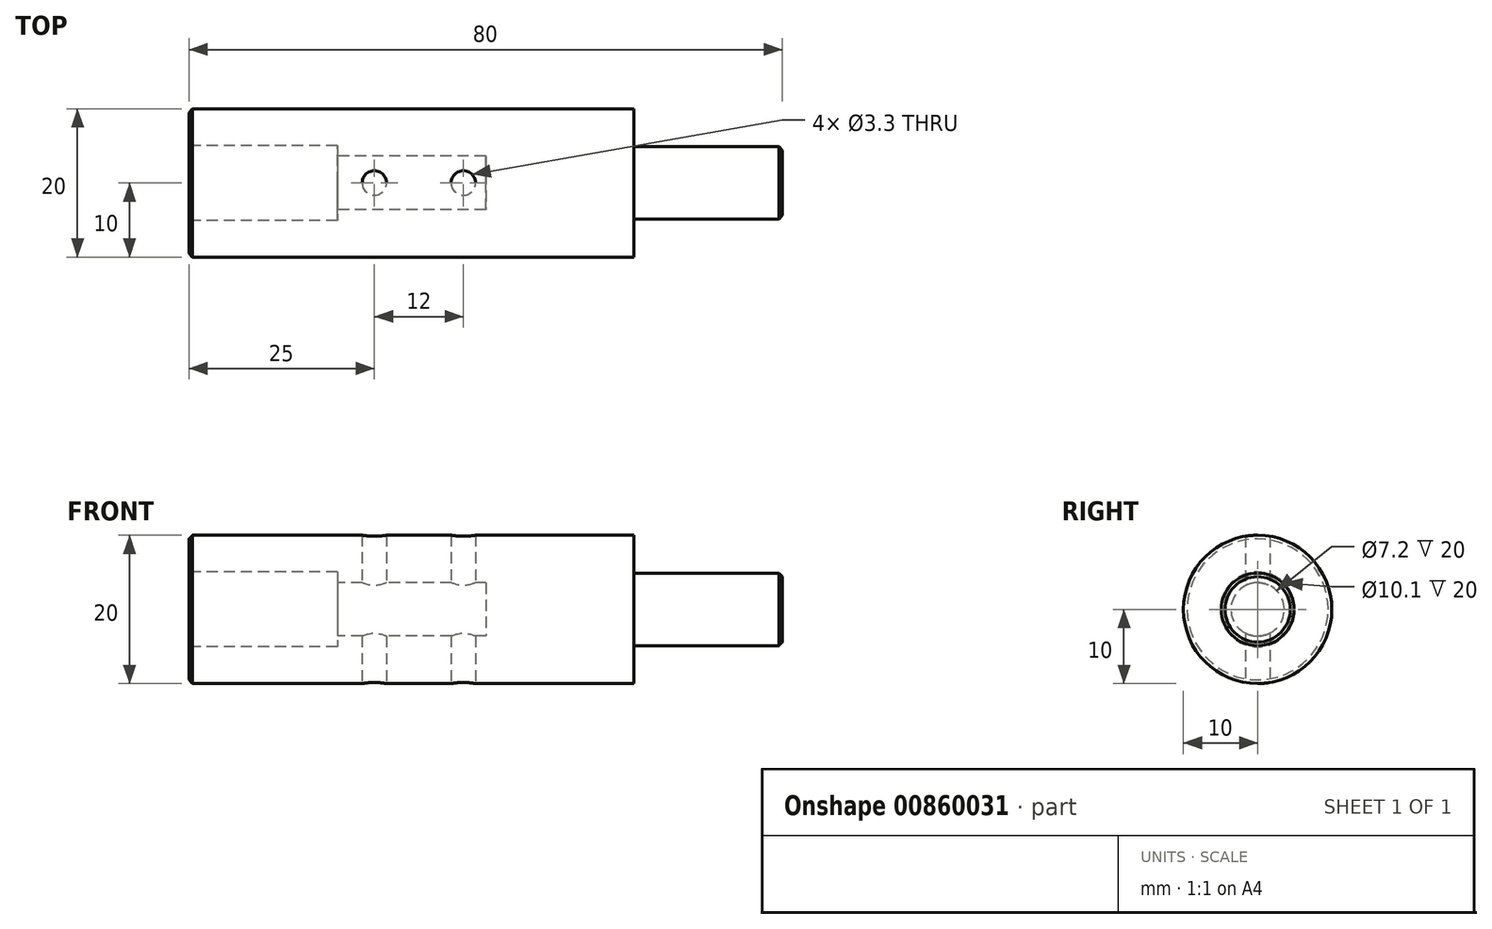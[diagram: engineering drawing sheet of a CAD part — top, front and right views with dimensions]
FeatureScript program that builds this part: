
annotation { "Feature Type Name" : "Feature", "Feature Type Description" : "" }
export const myFeature = defineFeature(function(context is Context, id is Id, definition is map)
    precondition{}
    {
        {
            var Q0;
            Q0=qCreatedBy(makeId("Front.planeOp"),FACE);
            var sketch = newSketch(context, id + "F0", { "sketchPlane" : qUnion([Q0])});
            skLineSegment(sketch, "E0", {"start": v(0, 0) * mm, "end": v(0, 3.6) * mm});
            skLineSegment(sketch, "E1", {"start": v(0, 3.6) * mm, "end": v(-20, 3.6) * mm});
            skLineSegment(sketch, "E2", {"start": v(-20, 3.6) * mm, "end": v(-20, 5.05) * mm});
            skLineSegment(sketch, "E3", {"start": v(-20, 5.05) * mm, "end": v(-40, 5.05) * mm});
            skLineSegment(sketch, "E4", {"start": v(-40, 5.05) * mm, "end": v(-40, 10) * mm});
            skLineSegment(sketch, "E5", {"start": v(-40, 10) * mm, "end": v(20, 10) * mm});
            skLineSegment(sketch, "E6", {"start": v(20, 10) * mm, "end": v(20, 4.9) * mm});
            skLineSegment(sketch, "E7", {"start": v(20, 4.9) * mm, "end": v(40, 4.9) * mm});
            skLineSegment(sketch, "E8", {"start": v(40, 4.9) * mm, "end": v(40, 0) * mm});
            skLineSegment(sketch, "E9", {"start": v(40, 0) * mm, "end": v(0, 0) * mm});
            skLineSegment(sketch, "E10", {"start": v(-51.87, 0) * mm, "end": v(49.04, 0) * mm, "construction": true});
            skSolve(sketch);
        }
        {
            var Q0;
            Q0=makeQuery(id+"F0.imprint","IMPRINT",FACE,{"disambiguationData":[TD([[makeQuery(id+"F0.imprint","IMPRINT",EDGE,{"derivedFrom":sQuery(id+"F0.wireOp",EDGE,"E0")}),-1.0]])]});
            var Q1;
            Q1=sQuery(id+"F0.wireOp",EDGE,"E10");
            revolve(context, id + "F1", {"surfaceOperationType" : NewSurfaceOperationType.NEW, "entities" : qUnion([Q0]), "axis" : qUnion([Q1]), "revolveType" : RevolveType.FULL});
        }
        {
            var Q0;
            Q0=qCreatedBy(makeId("Top.planeOp"),FACE);
            cPlane(context, id + "F2", {"entities" : qUnion([Q0]), "cplaneType" : CPlaneType.OFFSET, "offset" : 25 * mm, "oppositeDirection" : true, "width" : 150 * mm, "height" : 150 * mm});
        }
        {
            var Q0;
            Q0=makeQuery(id+"F1.opRevolve","SWEPT_EDGE",EDGE,{"disambiguationData":[OSD([sQuery(id+"F0.wireOp",EDGE,"E4"),sQuery(id+"F0.wireOp",EDGE,"E5")])]});
            var Q1;
            Q1=makeQuery(id+"F1.opRevolve","SWEPT_EDGE",EDGE,{"disambiguationData":[OSD([sQuery(id+"F0.wireOp",EDGE,"E7"),sQuery(id+"F0.wireOp",EDGE,"E8")])]});
            chamfer(context, id + "F3", {"entities" : qUnion([Q0, Q1]), "width" : 0.5 * mm, "tangentPropagation" : true});
        }
        {
            var Q0;
            Q0=qCreatedBy(id+"F2.planeOp",FACE);
            var sketch = newSketch(context, id + "F4", { "sketchPlane" : qUnion([Q0])});
            skPoint(sketch, "E11", {"position": v(-3, 0) * mm});
            skPoint(sketch, "E12", {"position": v(-15, 0) * mm});
            skSolve(sketch);
        }
        {
            var Q0;
            Q0=sQuery(id+"F4.wireOp",VERTEX,"E12");
            var Q1;
            Q1=sQuery(id+"F4.wireOp",VERTEX,"E11");
            var Q2;
            Q2=makeQuery(id+"F1.opRevolve","SWEPT_BODY",BODY,{"disambiguationData":[OSD([sQuery(id+"F0.wireOp",EDGE,"E0"),sQuery(id+"F0.wireOp",EDGE,"E1"),sQuery(id+"F0.wireOp",EDGE,"E2"),sQuery(id+"F0.wireOp",EDGE,"E3"),sQuery(id+"F0.wireOp",EDGE,"E4"),sQuery(id+"F0.wireOp",EDGE,"E5"),sQuery(id+"F0.wireOp",EDGE,"E6"),sQuery(id+"F0.wireOp",EDGE,"E7"),sQuery(id+"F0.wireOp",EDGE,"E8"),sQuery(id+"F0.wireOp",EDGE,"E9")])]});
            hole(context, id + "F5", {"style" : HoleStyle.SIMPLE, "endStyle" : HoleEndStyle.THROUGH, "oppositeDirection" : true, "standardTappedOrClearance" : lookupTablePath({ "standard" : "ISO", "engagement" : "75%", "pitch" : "0.7 mm", "size" : "M4", "type" : "Tapped" }), "standardBlindInLast" : lookupTablePath({ "standard" : "ISO", "engagement" : "75%", "pitch" : "0.7 mm", "size" : "M4", "type" : "Tapped" }), "holeDiameter" : 3.3 * mm, "majorDiameter" : 4 * mm, "showTappedDepth" : true, "isTappedThrough" : true, "tappedDepth" : 3.9 * mm, "tapClearance" : 3, "locations" : qUnion([Q0, Q1]), "scope" : qUnion([Q2])});
        }
    });
